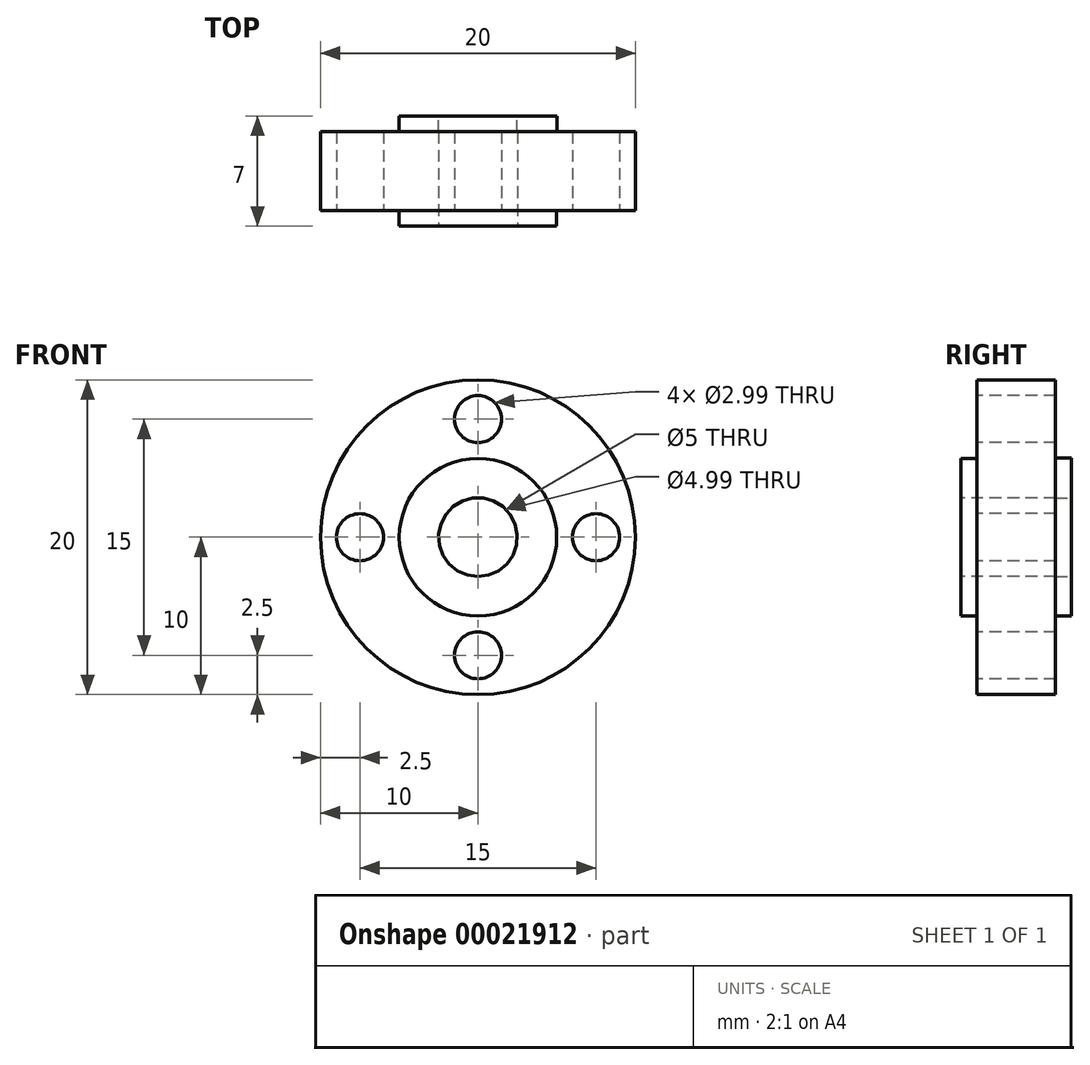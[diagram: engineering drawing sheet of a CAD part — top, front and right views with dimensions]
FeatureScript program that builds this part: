
annotation { "Feature Type Name" : "Feature", "Feature Type Description" : "" }
export const myFeature = defineFeature(function(context is Context, id is Id, definition is map)
    precondition{}
    {
        {
            var Q0;
            Q0=qCreatedBy(makeId("Front.planeOp"),FACE);
            var sketch = newSketch(context, id + "F0", { "sketchPlane" : qUnion([Q0])});
            skCircle(sketch, "E0", {"center": v(0, 0) * mm, "radius": 10 * mm});
            skSolve(sketch);
        }
        {
            var Q0;
            Q0 = qSketchRegion(id + "F0", true);
            extrude(context, id + "F1", {"entities" : qUnion([Q0]), "depth" : 5 * mm});
        }
        {
            var Q0;
            Q0=makeQuery(id+"F1.opExtrude","CAP_FACE",FACE,{"disambiguationData":[OSD([sQuery(id+"F0.wireOp",EDGE,"E0")])],"isStart":false});
            var sketch = newSketch(context, id + "F2", { "sketchPlane" : qUnion([Q0])});
            skCircle(sketch, "E1", {"center": v(0, 0) * mm, "radius": 5 * mm});
            skCircle(sketch, "E2", {"center": v(0, 0) * mm, "radius": 2.5 * mm});
            skSolve(sketch);
        }
        {
            var Q0;
            Q0=makeQuery(id+"F2.imprint","IMPRINT",FACE,{"disambiguationData":[TD([[makeQuery(id+"F2.imprint","IMPRINT",EDGE,{"derivedFrom":sQuery(id+"F2.wireOp",EDGE,"E2")}),1.0]])]});
            extrude(context, id + "F3", {"entities" : qUnion([Q0]), "operationType" : NewBodyOperationType.REMOVE, "endBound" : BoundingType.THROUGH_ALL, "oppositeDirection" : true, "depth" : 25.4 * mm});
        }
        {
            var Q0;
            Q0=makeQuery(id+"F2.imprint","IMPRINT",FACE,{"disambiguationData":[TD([[makeQuery(id+"F2.imprint","IMPRINT",EDGE,{"derivedFrom":sQuery(id+"F2.wireOp",EDGE,"E1")}),1.0]])]});
            var Q1;
            Q1=sQuery(id+"F2.wireOp",EDGE,"E1");
            extrude(context, id + "F4", {"entities" : qUnion([Q0]), "operationType" : NewBodyOperationType.ADD, "surfaceEntities" : qUnion([Q1]), "depth" : 1 * mm});
        }
        {
            var Q0;
            Q0=makeQuery(id+"F1.opExtrude","CAP_FACE",FACE,{"disambiguationData":[OSD([sQuery(id+"F0.wireOp",EDGE,"E0")])],"isStart":true});
            var sketch = newSketch(context, id + "F5", { "sketchPlane" : qUnion([Q0])});
            skCircle(sketch, "E3", {"center": v(0, 0) * mm, "radius": 5.02 * mm});
            skSolve(sketch);
        }
        {
            var Q0;
            Q0 = qSketchRegion(id + "F5", true);
            extrude(context, id + "F6", {"entities" : qUnion([Q0]), "operationType" : NewBodyOperationType.ADD, "depth" : 1 * mm});
        }
        {
            var Q0;
            Q0=makeQuery(id+"F6.opExtrude","CAP_FACE",FACE,{"disambiguationData":[OSD([sQuery(id+"F5.wireOp",EDGE,"E3")])],"isStart":false});
            var sketch = newSketch(context, id + "F7", { "sketchPlane" : qUnion([Q0])});
            skCircle(sketch, "E4", {"center": v(0, 0) * mm, "radius": 2.5 * mm});
            skSolve(sketch);
        }
        {
            var Q0;
            Q0 = qSketchRegion(id + "F7", true);
            extrude(context, id + "F8", {"entities" : qUnion([Q0]), "operationType" : NewBodyOperationType.REMOVE, "endBound" : BoundingType.THROUGH_ALL, "oppositeDirection" : true, "depth" : 25.4 * mm});
        }
        {
            var Q0;
            Q0=makeQuery(id+"F2.imprint","IMPRINT",FACE,{"disambiguationData":[TD([[makeQuery(id+"F2.imprint","IMPRINT",EDGE,{"derivedFrom":sQuery(id+"F2.wireOp",EDGE,"E1")}),-1.0]])]});
            var sketch = newSketch(context, id + "F9", { "sketchPlane" : qUnion([Q0])});
            skCircle(sketch, "E5", {"center": v(0, 7.5) * mm, "radius": 1.5 * mm});
            skCircle(sketch, "E6.1.0", {"center": v(-7.5, 0) * mm, "radius": 1.5 * mm});
            skCircle(sketch, "E6.2.0", {"center": v(0, -7.5) * mm, "radius": 1.5 * mm});
            skCircle(sketch, "E6.3.0", {"center": v(7.5, 0) * mm, "radius": 1.5 * mm});
            skPoint(sketch, "E6.center", {"position": v(0, 0) * mm});
            skSolve(sketch);
        }
        {
            var Q0;
            Q0 = qSketchRegion(id + "F9", true);
            extrude(context, id + "F10", {"entities" : qUnion([Q0]), "operationType" : NewBodyOperationType.REMOVE, "endBound" : BoundingType.THROUGH_ALL, "oppositeDirection" : true, "depth" : 25.4 * mm});
        }
    });
